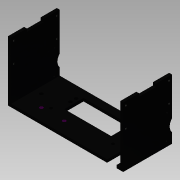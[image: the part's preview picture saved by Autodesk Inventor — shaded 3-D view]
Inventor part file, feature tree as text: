
AUTODESK INVENTOR PART (.ipt)
format: ipt  version: 2015 SP1 (Build 190203100, 203)  size: 241,664 bytes
history: native  units: mm
features: reference x18, extrude x12, sketch x11, plane x1
ambient origin geometry x8: Origin, YZ Plane, XZ Plane, XY Plane, X Axis, Y Axis, Z Axis, Center Point
bodies: Solid1 (feature_tree)
feature tree (42):
  sketch  "Sketch1"  dims[d0=120.812mm d1=51.214111mm]
  extrude  "Extrusion1"  Depth=51.214111mm
  extrude  "Extrusion2"  Depth=63.0mm TaperAngle=0.0deg
  plane  "Work Plane2"
  extrude  "Extrusion3"  Depth=3.0mm
  extrude  "Extrusion4"  [1 undecoded]
  extrude  "Extrusion5"  Depth=3.5mm
  extrude  "Extrusion7"  Depth=3.5mm
  extrude  "Extrusion8"  Depth=17.5mm
  extrude  "Extrusion9"  Depth=10.0mm TaperAngle=0.0deg
  extrude  "Extrusion11"  Depth=10.0mm TaperAngle=0.0deg
  extrude  "Extrusion12"  Depth=3.5mm
  sketch  "Sketch17"  dims[d31=3.5mm d32=3.5mm]
  extrude  "Extrusion13"  Depth=10.0mm
  extrude  "Extrusion14"  Depth=10.0mm TaperAngle=0.0deg
  sketch  "Sketch2"  dims[d4=3.0mm d5=0.0mm d6=63.0mm d7=0.0mm]
  reference  "Reference1"
  reference  "Reference2"
  reference  "Reference3"
  reference  "Reference4"
  sketch  "Sketch4"  dims[d8=3.0mm d9=3.0mm]
  sketch  "Sketch6"  dims[d10=114.812mm d11=-18.417445mm]
  reference  "Reference5"
  reference  "Reference6"
  sketch  "Sketch9"  dims[d12=3.5mm d13=3.5mm]
  reference  "Reference8"
  reference  "Reference9"
  reference  "Reference10"
  reference  "Reference11"
  sketch  "Sketch10"  dims[d14=3.5mm d15=3.5mm]
  sketch  "Sketch11"  dims[d16=10.0mm d17=0.0mm d18=17.5mm]
  reference  "Reference13"
  reference  "Reference14"
  reference  "Reference15"
  sketch  "Sketch15"  dims[d19=3.0mm d20=0.0mm d21=10.0mm d22=0.0mm]
  reference  "Reference21"
  sketch  "Sketch16"  dims[d25=200.0mm d26=0.0mm d29=10.0mm d30=0.0mm]
  reference  "Reference22"
  reference  "Reference23"
  reference  "Reference24"
  reference  "Reference25"
  sketch  "Sketch18"  dims[d33=2.0mm d34=2.0mm d35=10.0mm d36=0.0mm d37=2.0mm d38=2.0mm d39=90.0deg d47=10.0mm d48=0.0mm d49=10.0mm d50=17.5mm d51=10.0mm d52=0.0mm d53=3.5mm d54=6.0mm d55=6.0mm d56=20.0mm d59=5.0mm d60=2.0mm d61=5.5mm d62=5.714111mm d63=10.0mm d64=0.0mm d65=10.0mm d66=0.0mm]
note: 1 required parameter value undecoded (feature->parameter linkage not recoverable at this tier; creation-order binding heuristic only, values carry confidence <= 0.55)
